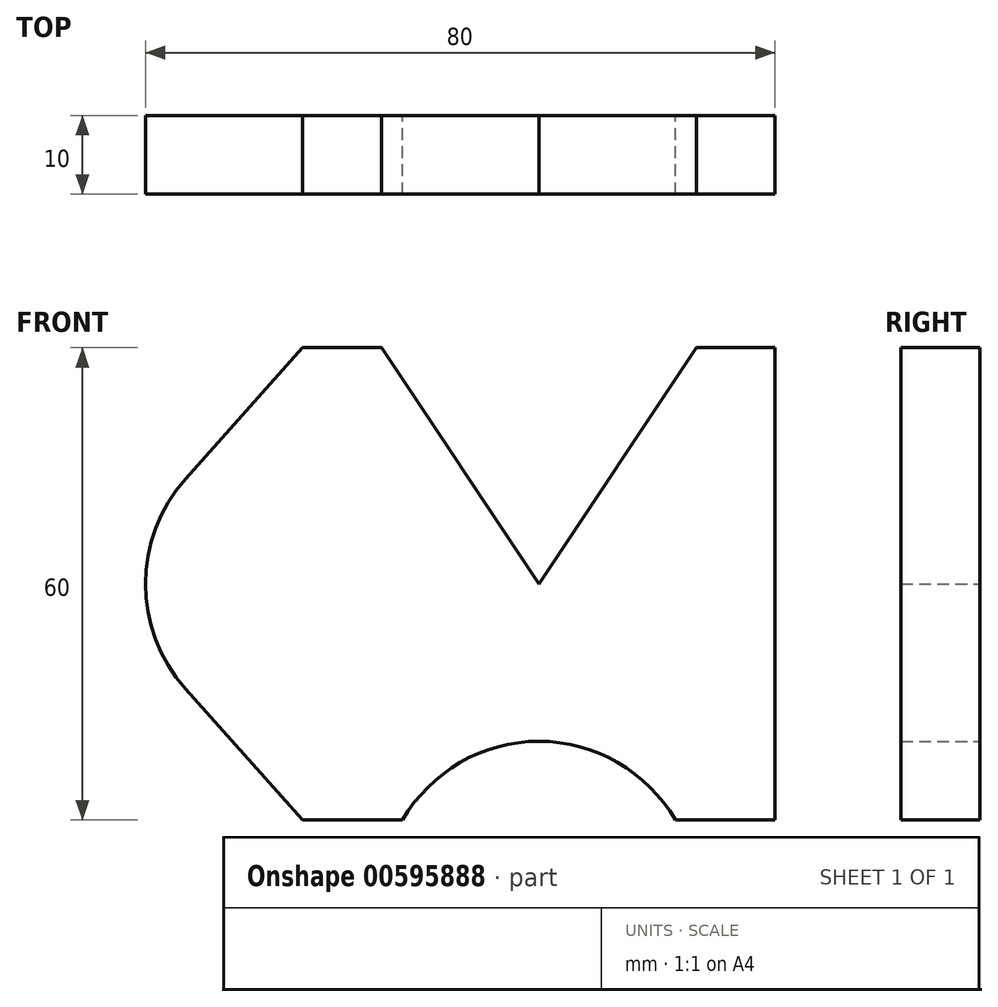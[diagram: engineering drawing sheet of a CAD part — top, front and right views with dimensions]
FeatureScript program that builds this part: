
annotation { "Feature Type Name" : "Feature", "Feature Type Description" : "" }
export const myFeature = defineFeature(function(context is Context, id is Id, definition is map)
    precondition{}
    {
        {
            var Q0;
            Q0=qCreatedBy(makeId("Front.planeOp"),FACE);
            var sketch = newSketch(context, id + "F0", { "sketchPlane" : qUnion([Q0])});
            skLineSegment(sketch, "E0", {"start": v(-30, 30) * mm, "end": v(-20, 30) * mm});
            skLineSegment(sketch, "E1", {"start": v(-20, 30) * mm, "end": v(0, 0) * mm});
            skLineSegment(sketch, "E2", {"start": v(0, 0) * mm, "end": v(20, 30) * mm});
            skLineSegment(sketch, "E3", {"start": v(20, 30) * mm, "end": v(30, 30) * mm});
            skLineSegment(sketch, "E4", {"start": v(30, 30) * mm, "end": v(30, -30) * mm});
            skLineSegment(sketch, "E5", {"start": v(30, -30) * mm, "end": v(17.32, -30) * mm});
            skArc(sketch, "E6", {"start": v(17.32, -30) * mm, "mid": v(0, -20) * mm, "end": v(-17.32, -30) * mm});
            skLineSegment(sketch, "E7", {"start": v(-30, 30) * mm, "end": v(-44.9, 13.33) * mm});
            skLineSegment(sketch, "E8", {"start": v(-17.32, -30) * mm, "end": v(-30, -30) * mm});
            skLineSegment(sketch, "E9", {"start": v(-30, -30) * mm, "end": v(-44.9, -13.33) * mm});
            skArc(sketch, "E10", {"start": v(-44.9, 13.33) * mm, "mid": v(-50, 0) * mm, "end": v(-44.9, -13.33) * mm});
            skSolve(sketch);
        }
        {
            var Q0;
            Q0=makeQuery(id+"F0.imprint","IMPRINT",FACE,{"disambiguationData":[TD([[makeQuery(id+"F0.imprint","IMPRINT",EDGE,{"derivedFrom":sQuery(id+"F0.wireOp",EDGE,"E0")}),-1.0]])]});
            extrude(context, id + "F1", {"entities" : qUnion([Q0]), "depth" : 10 * mm, "offsetDistance" : 25 * mm});
        }
    });
